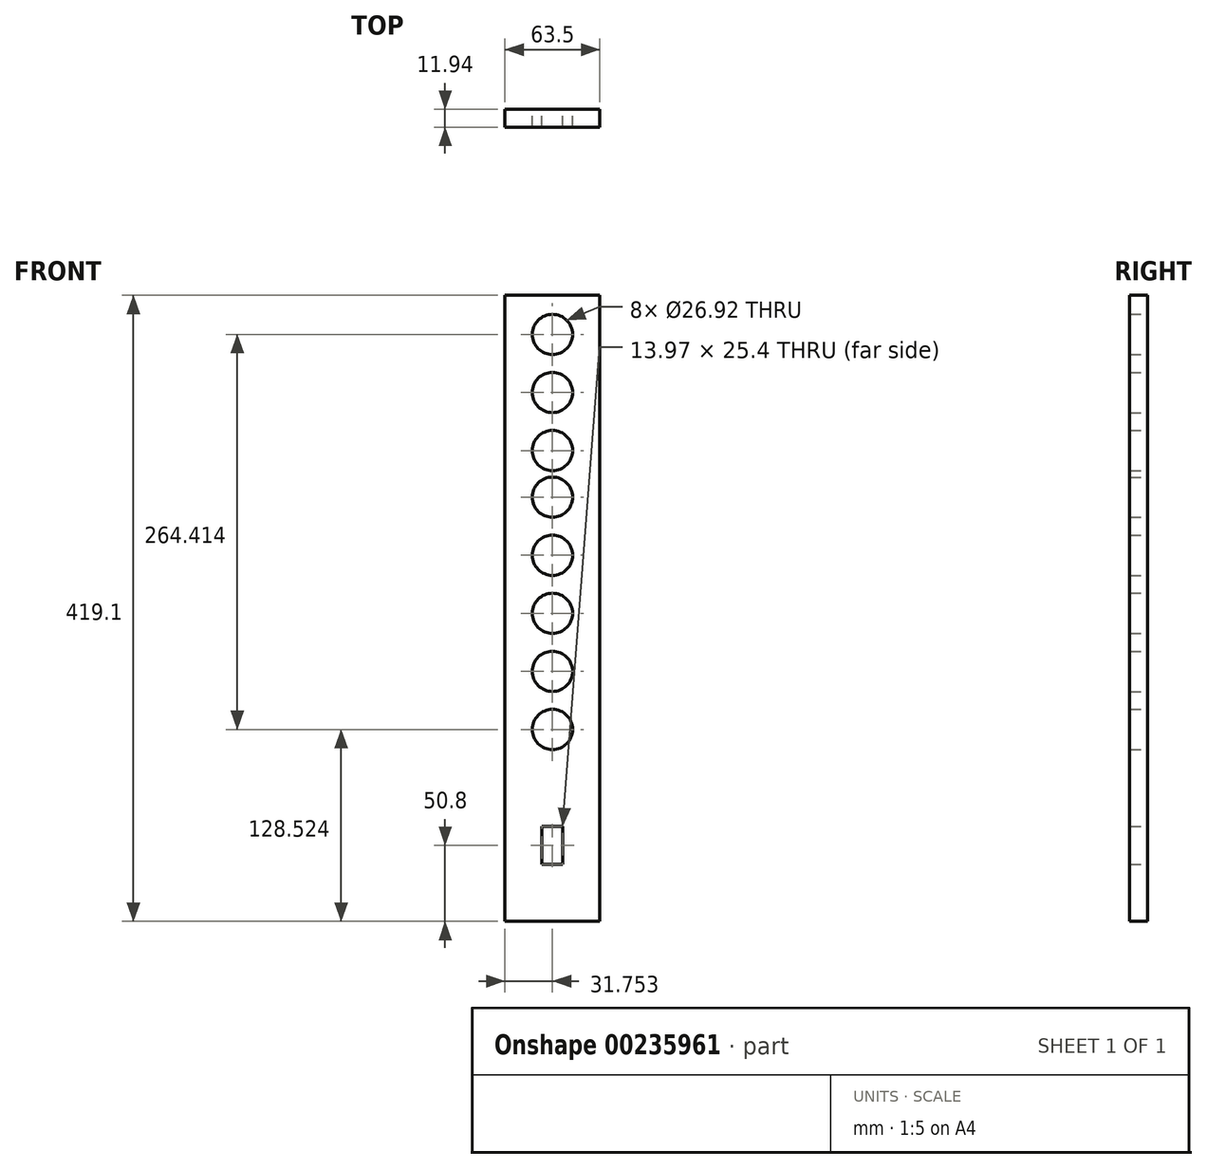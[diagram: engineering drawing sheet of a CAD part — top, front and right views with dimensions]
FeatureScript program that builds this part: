
annotation { "Feature Type Name" : "Feature", "Feature Type Description" : "" }
export const myFeature = defineFeature(function(context is Context, id is Id, definition is map)
    precondition{}
    {
        {
            var Q0;
            Q0=qCreatedBy(makeId("Front.planeOp"),FACE);
            var sketch = newSketch(context, id + "F0", { "sketchPlane" : qUnion([Q0])});
            skLineSegment(sketch, "E0", {"start": v(-70.52, -207.98) * mm, "end": v(-7.02, -207.98) * mm});
            skLineSegment(sketch, "E1", {"start": v(-70.52, -195.28) * mm, "end": v(-7.02, -195.28) * mm});
            skLineSegment(sketch, "E2", {"start": v(-70.52, -169.12) * mm, "end": v(-7.02, -169.12) * mm});
            skLineSegment(sketch, "E3", {"start": v(-70.52, -130.26) * mm, "end": v(-7.02, -130.26) * mm});
            skLineSegment(sketch, "E4", {"start": v(-70.52, -91.4) * mm, "end": v(-7.02, -91.4) * mm});
            skCircle(sketch, "E5", {"center": v(-38.77, -91.4) * mm, "radius": 13.46 * mm});
            skLineSegment(sketch, "E6", {"start": v(-70.52, -52.53) * mm, "end": v(-7.02, -52.53) * mm});
            skCircle(sketch, "E7", {"center": v(-38.77, -52.53) * mm, "radius": 13.46 * mm});
            skLineSegment(sketch, "E8", {"start": v(-70.52, -13.67) * mm, "end": v(-7.02, -13.67) * mm});
            skCircle(sketch, "E9", {"center": v(-38.77, -13.67) * mm, "radius": 13.46 * mm});
            skLineSegment(sketch, "E10", {"start": v(-70.52, 25.19) * mm, "end": v(-7.02, 25.19) * mm});
            skCircle(sketch, "E11", {"center": v(-38.77, 25.19) * mm, "radius": 13.46 * mm});
            skLineSegment(sketch, "E12", {"start": v(-70.52, 64.05) * mm, "end": v(-7.02, 64.05) * mm});
            skCircle(sketch, "E13", {"center": v(-38.77, 64.05) * mm, "radius": 13.46 * mm});
            skLineSegment(sketch, "E14", {"start": v(-70.52, 95.3) * mm, "end": v(-7.02, 95.3) * mm});
            skCircle(sketch, "E15", {"center": v(-38.77, 95.3) * mm, "radius": 13.46 * mm});
            skLineSegment(sketch, "E16", {"start": v(-70.52, 134.16) * mm, "end": v(-7.02, 134.16) * mm});
            skCircle(sketch, "E17", {"center": v(-38.77, 134.16) * mm, "radius": 13.46 * mm});
            skLineSegment(sketch, "E18", {"start": v(-70.52, 173.02) * mm, "end": v(-7.02, 173.02) * mm});
            skCircle(sketch, "E19", {"center": v(-38.77, 173.02) * mm, "radius": 13.46 * mm});
            skLineSegment(sketch, "E20", {"start": v(-70.52, 199.18) * mm, "end": v(-7.02, 199.18) * mm});
            skLineSegment(sketch, "E21", {"start": v(-7.02, 199.18) * mm, "end": v(-7.02, -207.98) * mm});
            skLineSegment(sketch, "E22", {"start": v(-70.52, 199.18) * mm, "end": v(-70.52, -207.98) * mm});
            skSolve(sketch);
        }
        {
            var Q0;
            {var subQ6=sQuery(id+"F0.wireOp",EDGE,"E20");Q0=makeQuery(id+"F0.imprint","IMPRINT",FACE,{"disambiguationData":[TD([[makeQuery(id+"F0.imprint","IMPRINT",EDGE,{"derivedFrom":subQ6}),-1.0]])]});}
            var Q1;
            {var subQ1=sQuery(id+"F0.wireOp",EDGE,"E16");var subQ6=sQuery(id+"F0.wireOp",EDGE,"E22");var subQ7=makeQuery(id+"F0.imprint","INTERSECT",VERTEX,{"derivedFrom":[subQ1,subQ6]});Q1=makeQuery(id+"F0.imprint","IMPRINT",FACE,{"disambiguationData":[TD([[makeQuery(id+"F0.imprint","IMPRINT",EDGE,{"disambiguationData":[TD([[subQ7,-1.0]])],"derivedFrom":subQ1}),1.0]])]});}
            var Q2;
            {var subQ1=sQuery(id+"F0.wireOp",EDGE,"E14");var subQ6=sQuery(id+"F0.wireOp",EDGE,"E22");var subQ11=makeQuery(id+"F0.imprint","INTERSECT",VERTEX,{"derivedFrom":[subQ1,subQ6]});Q2=makeQuery(id+"F0.imprint","IMPRINT",FACE,{"disambiguationData":[TD([[makeQuery(id+"F0.imprint","IMPRINT",EDGE,{"disambiguationData":[TD([[subQ11,-1.0]])],"derivedFrom":subQ1}),1.0]])]});}
            var Q3;
            {var subQ1=sQuery(id+"F0.wireOp",EDGE,"E12");var subQ4=sQuery(id+"F0.wireOp",EDGE,"E22");var subQ5=makeQuery(id+"F0.imprint","INTERSECT",VERTEX,{"derivedFrom":[subQ1,subQ4]});Q3=makeQuery(id+"F0.imprint","IMPRINT",FACE,{"disambiguationData":[TD([[makeQuery(id+"F0.imprint","IMPRINT",EDGE,{"disambiguationData":[TD([[subQ5,-1.0]])],"derivedFrom":subQ1}),1.0]])]});}
            var Q4;
            {var subQ1=sQuery(id+"F0.wireOp",EDGE,"E10");var subQ6=sQuery(id+"F0.wireOp",EDGE,"E22");var subQ11=makeQuery(id+"F0.imprint","INTERSECT",VERTEX,{"derivedFrom":[subQ1,subQ6]});Q4=makeQuery(id+"F0.imprint","IMPRINT",FACE,{"disambiguationData":[TD([[makeQuery(id+"F0.imprint","IMPRINT",EDGE,{"disambiguationData":[TD([[subQ11,-1.0]])],"derivedFrom":subQ1}),1.0]])]});}
            var Q5;
            {var subQ1=sQuery(id+"F0.wireOp",EDGE,"E8");var subQ8=sQuery(id+"F0.wireOp",EDGE,"E22");var subQ12=makeQuery(id+"F0.imprint","INTERSECT",VERTEX,{"derivedFrom":[subQ1,subQ8]});Q5=makeQuery(id+"F0.imprint","IMPRINT",FACE,{"disambiguationData":[TD([[makeQuery(id+"F0.imprint","IMPRINT",EDGE,{"disambiguationData":[TD([[subQ12,-1.0]])],"derivedFrom":subQ1}),1.0]])]});}
            var Q6;
            {var subQ1=sQuery(id+"F0.wireOp",EDGE,"E6");var subQ6=sQuery(id+"F0.wireOp",EDGE,"E22");var subQ11=makeQuery(id+"F0.imprint","INTERSECT",VERTEX,{"derivedFrom":[subQ1,subQ6]});Q6=makeQuery(id+"F0.imprint","IMPRINT",FACE,{"disambiguationData":[TD([[makeQuery(id+"F0.imprint","IMPRINT",EDGE,{"disambiguationData":[TD([[subQ11,-1.0]])],"derivedFrom":subQ1}),1.0]])]});}
            var Q7;
            {var subQ1=sQuery(id+"F0.wireOp",EDGE,"E4");var subQ6=sQuery(id+"F0.wireOp",EDGE,"E22");var subQ11=makeQuery(id+"F0.imprint","INTERSECT",VERTEX,{"derivedFrom":[subQ1,subQ6]});Q7=makeQuery(id+"F0.imprint","IMPRINT",FACE,{"disambiguationData":[TD([[makeQuery(id+"F0.imprint","IMPRINT",EDGE,{"disambiguationData":[TD([[subQ11,-1.0]])],"derivedFrom":subQ1}),1.0]])]});}
            var Q8;
            {var subQ1=sQuery(id+"F0.wireOp",EDGE,"E3");var subQ6=sQuery(id+"F0.wireOp",EDGE,"E22");var subQ11=makeQuery(id+"F0.imprint","INTERSECT",VERTEX,{"derivedFrom":[subQ1,subQ6]});Q8=makeQuery(id+"F0.imprint","IMPRINT",FACE,{"disambiguationData":[TD([[makeQuery(id+"F0.imprint","IMPRINT",EDGE,{"disambiguationData":[TD([[subQ11,-1.0]])],"derivedFrom":subQ1}),1.0]])]});}
            var Q9;
            {var subQ1=sQuery(id+"F0.wireOp",EDGE,"E2");var subQ6=sQuery(id+"F0.wireOp",EDGE,"E22");var subQ12=makeQuery(id+"F0.imprint","INTERSECT",VERTEX,{"derivedFrom":[subQ1,subQ6]});Q9=makeQuery(id+"F0.imprint","IMPRINT",FACE,{"disambiguationData":[TD([[makeQuery(id+"F0.imprint","IMPRINT",EDGE,{"disambiguationData":[TD([[subQ12,-1.0]])],"derivedFrom":subQ1}),1.0]])]});}
            var Q10;
            {var subQ8=sQuery(id+"F0.wireOp",EDGE,"E1");Q10=makeQuery(id+"F0.imprint","IMPRINT",FACE,{"disambiguationData":[TD([[makeQuery(id+"F0.imprint","IMPRINT",EDGE,{"derivedFrom":subQ8}),1.0]])]});}
            var Q11;
            {var subQ0=sQuery(id+"F0.wireOp",EDGE,"E0");Q11=makeQuery(id+"F0.imprint","IMPRINT",FACE,{"disambiguationData":[TD([[makeQuery(id+"F0.imprint","IMPRINT",EDGE,{"derivedFrom":subQ0}),1.0]])]});}
            extrude(context, id + "F1", {"entities" : qUnion([Q0, Q1, Q2, Q3, Q4, Q5, Q6, Q7, Q8, Q9, Q10, Q11]), "depth" : 11.94 * mm});
        }
        {
            var Q0;
            Q0=makeQuery(id+"F1.opExtrude","CAP_FACE",FACE,{"disambiguationData":[OSD([sQuery(id+"F0.wireOp",EDGE,"E0"),sQuery(id+"F0.wireOp",EDGE,"E5"),sQuery(id+"F0.wireOp",EDGE,"E7"),sQuery(id+"F0.wireOp",EDGE,"E9"),sQuery(id+"F0.wireOp",EDGE,"E11"),sQuery(id+"F0.wireOp",EDGE,"E13"),sQuery(id+"F0.wireOp",EDGE,"E15"),sQuery(id+"F0.wireOp",EDGE,"E17"),sQuery(id+"F0.wireOp",EDGE,"E19"),sQuery(id+"F0.wireOp",EDGE,"E20"),sQuery(id+"F0.wireOp",EDGE,"E21"),sQuery(id+"F0.wireOp",EDGE,"E22")])],"isStart":true});
            var sketch = newSketch(context, id + "F2", { "sketchPlane" : qUnion([Q0])});
            skLineSegment(sketch, "E23", {"start": v(7.02, -130.26) * mm, "end": v(70.52, -130.26) * mm});
            skLineSegment(sketch, "E24", {"start": v(38.77, -141.18) * mm, "end": v(70.52, -141.18) * mm});
            skLineSegment(sketch, "E25", {"start": v(38.77, -141.18) * mm, "end": v(7.02, -141.18) * mm});
            skLineSegment(sketch, "E26", {"start": v(31.78, -181.82) * mm, "end": v(45.75, -181.82) * mm});
            skLineSegment(sketch, "E27", {"start": v(31.78, -181.82) * mm, "end": v(31.78, -156.42) * mm});
            skLineSegment(sketch, "E28", {"start": v(45.75, -181.82) * mm, "end": v(45.75, -156.42) * mm});
            skLineSegment(sketch, "E29", {"start": v(45.75, -156.42) * mm, "end": v(31.78, -156.42) * mm});
            skSolve(sketch);
        }
        {
            var Q0;
            Q0 = qSketchRegion(id + "F2", true);
            extrude(context, id + "F3", {"entities" : qUnion([Q0]), "operationType" : NewBodyOperationType.REMOVE, "oppositeDirection" : true, "depth" : 25.4 * mm});
        }
        {
            var Q0;
            Q0=makeQuery(id+"F1.opExtrude","SWEPT_FACE",FACE,{"disambiguationData":[OSD([sQuery(id+"F0.wireOp",EDGE,"E0")])]});
            var sketch = newSketch(context, id + "F4", { "sketchPlane" : qUnion([Q0])});
            skLineSegment(sketch, "E30.0", {"start": v(-70.52, 11.94) * mm, "end": v(-7.02, 11.94) * mm});
            skLineSegment(sketch, "E31.0", {"start": v(-7.02, 11.94) * mm, "end": v(-7.02, 0) * mm});
            skLineSegment(sketch, "E32.0", {"start": v(-70.52, 0) * mm, "end": v(-7.02, 0) * mm});
            skLineSegment(sketch, "E33.0", {"start": v(-70.52, 11.94) * mm, "end": v(-70.52, 0) * mm});
            skSolve(sketch);
        }
        {
            var Q0;
            Q0=makeQuery(id+"F4.imprint","IMPRINT",FACE,{"disambiguationData":[TD([[makeQuery(id+"F4.imprint","IMPRINT",EDGE,{"derivedFrom":sQuery(id+"F4.wireOp",EDGE,"E30.0")}),-1.0]])]});
            extrude(context, id + "F5", {"entities" : qUnion([Q0]), "operationType" : NewBodyOperationType.ADD, "depth" : 11.94 * mm});
        }
    });
